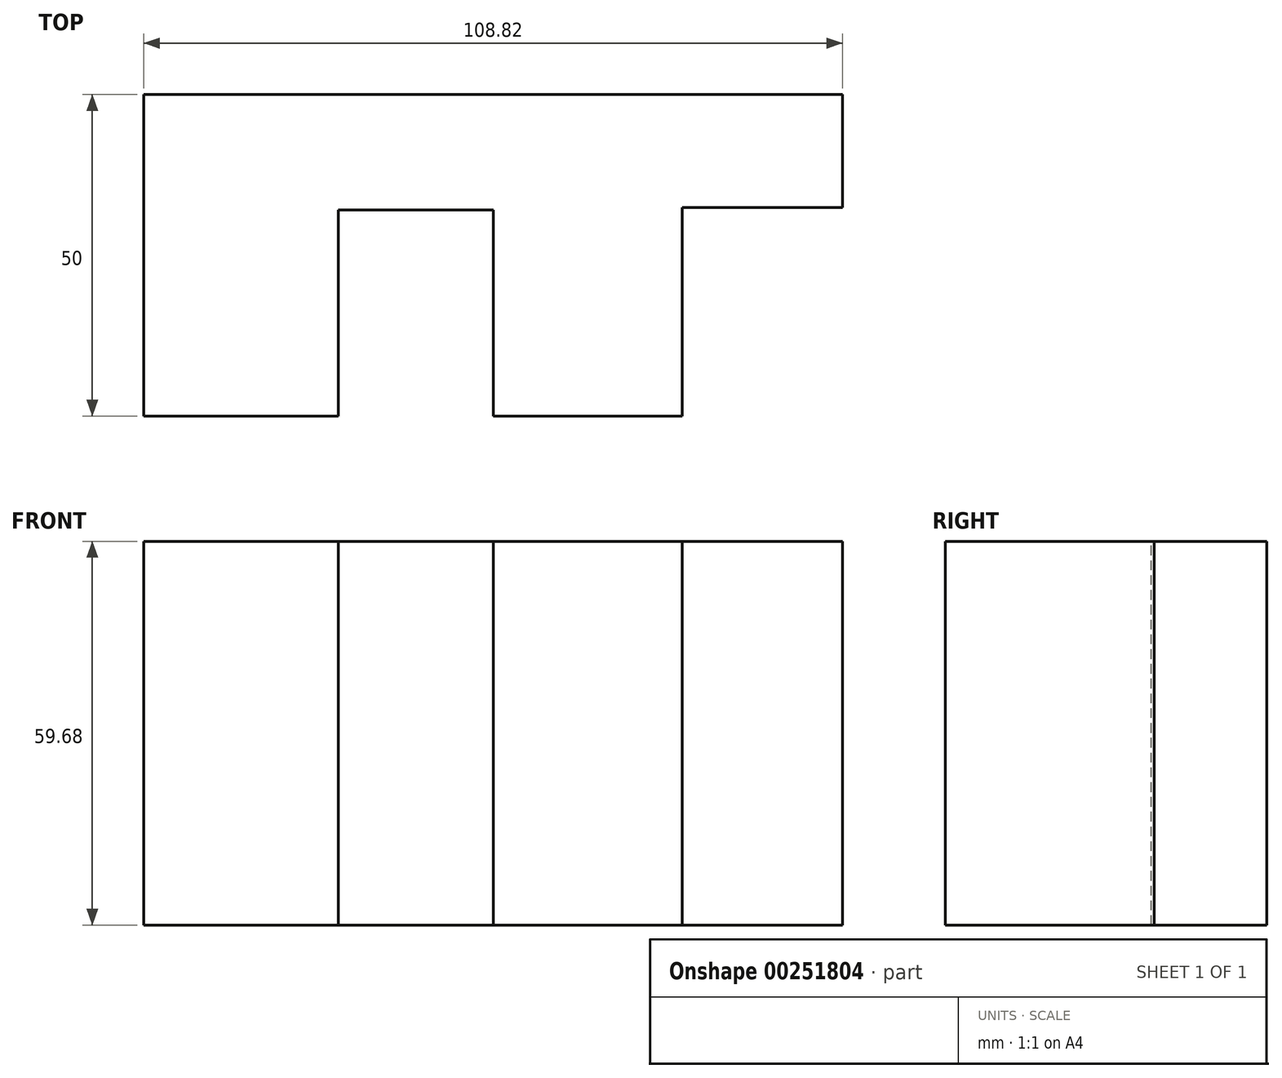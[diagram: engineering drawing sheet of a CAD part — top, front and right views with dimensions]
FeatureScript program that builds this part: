
annotation { "Feature Type Name" : "Feature", "Feature Type Description" : "" }
export const myFeature = defineFeature(function(context is Context, id is Id, definition is map)
    precondition{}
    {
        {
            var Q0;
            Q0=qCreatedBy(makeId("Front.planeOp"),FACE);
            var sketch = newSketch(context, id + "F0", { "sketchPlane" : qUnion([Q0])});
            skLineSegment(sketch, "E0.bottom", {"start": v(-54.41, -29.84) * mm, "end": v(54.41, -29.84) * mm});
            skLineSegment(sketch, "E0.top", {"start": v(-54.41, 29.84) * mm, "end": v(54.41, 29.84) * mm});
            skLineSegment(sketch, "E0.left", {"start": v(-54.41, -29.84) * mm, "end": v(-54.41, 29.84) * mm});
            skLineSegment(sketch, "E0.right", {"start": v(54.41, -29.84) * mm, "end": v(54.41, 29.84) * mm});
            skPoint(sketch, "E0.middle", {"position": v(0, 0) * mm});
            skSolve(sketch);
        }
        {
            var Q0;
            Q0 = qSketchRegion(id + "F0", true);
            extrude(context, id + "F1", {"entities" : qUnion([Q0]), "oppositeDirection" : true, "depth" : 50 * mm});
        }
        {
            var Q0;
            Q0=makeQuery(id+"F1.opExtrude","SWEPT_FACE",FACE,{"disambiguationData":[OSD([sQuery(id+"F0.wireOp",EDGE,"E0.right")])]});
            var sketch = newSketch(context, id + "F2", { "sketchPlane" : qUnion([Q0])});
            skLineSegment(sketch, "E1", {"start": v(32.46, 29.84) * mm, "end": v(32.46, -29.84) * mm});
            skSolve(sketch);
        }
        {
            var Q0;
            {var subQ0=sQuery(id+"F2.wireOp",EDGE,"E1");Q0=makeQuery(id+"F2.imprint","IMPRINT",FACE,{"disambiguationData":[TD([[makeQuery(id+"F2.imprint","IMPRINT",EDGE,{"derivedFrom":subQ0}),-1.0]])]});}
            extrude(context, id + "F3", {"entities" : qUnion([Q0]), "operationType" : NewBodyOperationType.REMOVE, "oppositeDirection" : true, "depth" : 25 * mm});
        }
        {
            var Q0;
            Q0=makeQuery(id+"F1.opExtrude","SWEPT_FACE",FACE,{"disambiguationData":[OSD([sQuery(id+"F0.wireOp",EDGE,"E0.top")])]});
            var sketch = newSketch(context, id + "F4", { "sketchPlane" : qUnion([Q0])});
            skLineSegment(sketch, "E2", {"start": v(0, 0) * mm, "end": v(0, 32.02) * mm});
            skLineSegment(sketch, "E3", {"start": v(0, 32.02) * mm, "end": v(-24.13, 32.02) * mm});
            skLineSegment(sketch, "E4", {"start": v(-24.13, 32.02) * mm, "end": v(-24.13, 0) * mm});
            skSolve(sketch);
        }
        {
            var Q0;
            Q0 = qSketchRegion(id + "F4", true);
            var Q1;
            {var subQ0=sQuery(id+"F4.wireOp",EDGE,"E2");Q1=makeQuery(id+"F4.imprint","IMPRINT",FACE,{"disambiguationData":[TD([[makeQuery(id+"F4.imprint","IMPRINT",EDGE,{"derivedFrom":subQ0}),1.0]])]});}
            extrude(context, id + "F5", {"entities" : qUnion([Q0, Q1]), "operationType" : NewBodyOperationType.REMOVE, "depth" : 25 * mm});
        }
        {
            var Q0;
            {var subQ0=sQuery(id+"F4.wireOp",EDGE,"E2");Q0=makeQuery(id+"F4.imprint","IMPRINT",FACE,{"disambiguationData":[TD([[makeQuery(id+"F4.imprint","IMPRINT",EDGE,{"derivedFrom":subQ0}),1.0]])]});}
            extrude(context, id + "F6", {"entities" : qUnion([Q0]), "operationType" : NewBodyOperationType.REMOVE, "oppositeDirection" : true, "depth" : 60 * mm});
        }
    });
